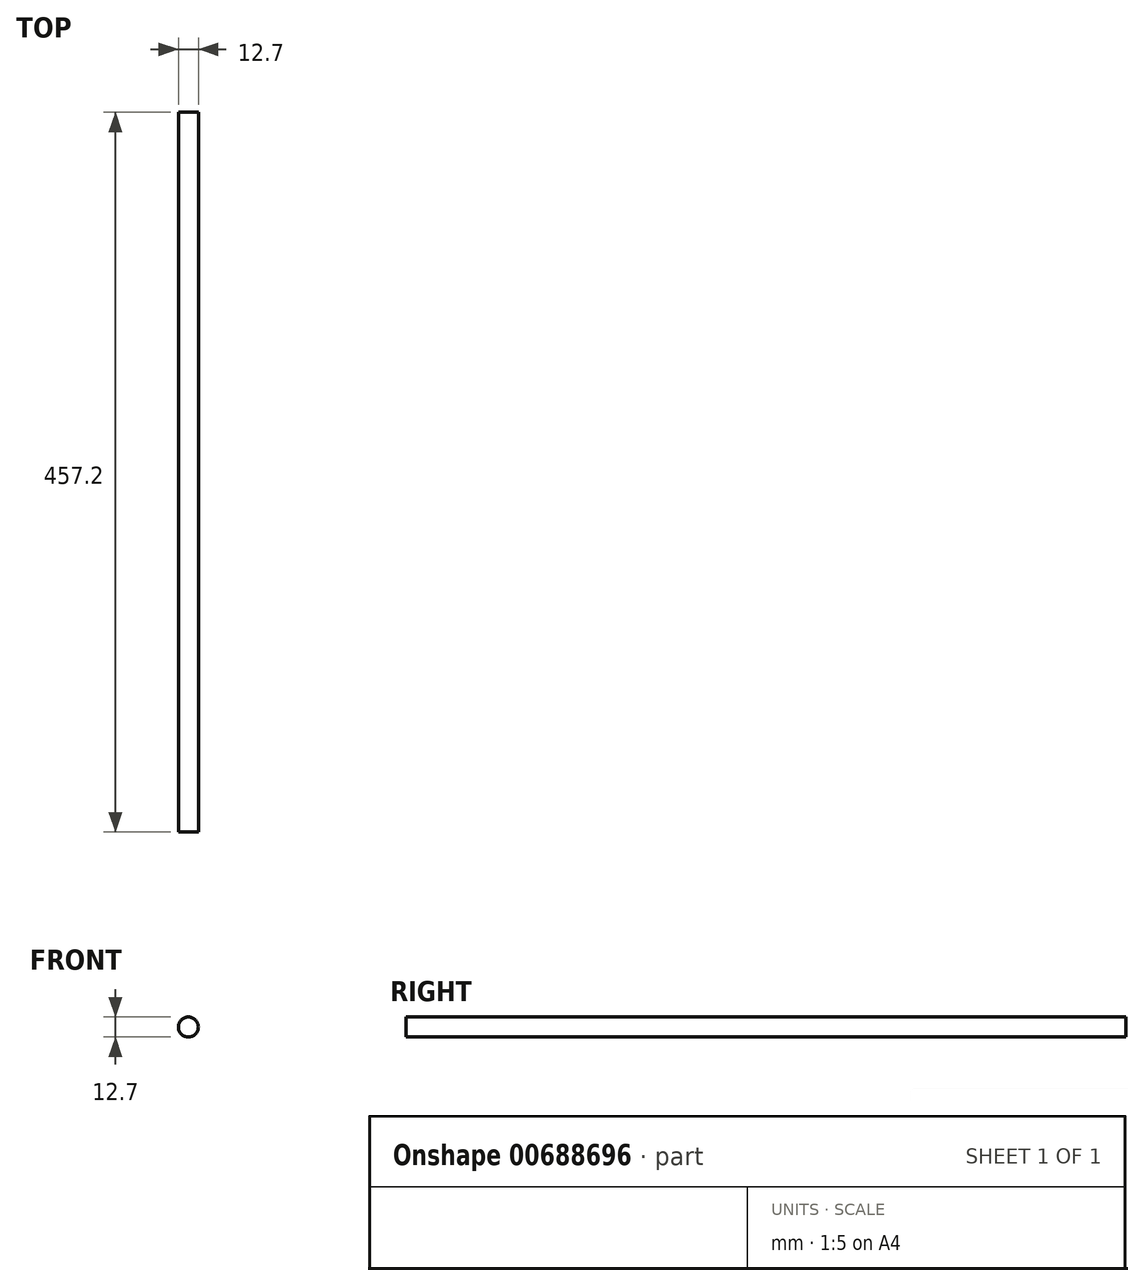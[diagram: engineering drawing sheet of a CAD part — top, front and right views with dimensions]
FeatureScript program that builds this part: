
annotation { "Feature Type Name" : "Feature", "Feature Type Description" : "" }
export const myFeature = defineFeature(function(context is Context, id is Id, definition is map)
    precondition{}
    {
        {
            var Q0;
            Q0=qCreatedBy(makeId("Front.planeOp"),FACE);
            var sketch = newSketch(context, id + "F0", { "sketchPlane" : qUnion([Q0])});
            skCircle(sketch, "E0", {"center": v(0, 0) * mm, "radius": 6.35 * mm});
            skSolve(sketch);
        }
        {
            var Q0;
            Q0 = qSketchRegion(id + "F0", true);
            extrude(context, id + "F1", {"entities" : qUnion([Q0]), "depth" : 457.2 * mm, "offsetDistance" : 25.4 * mm});
        }
    });
